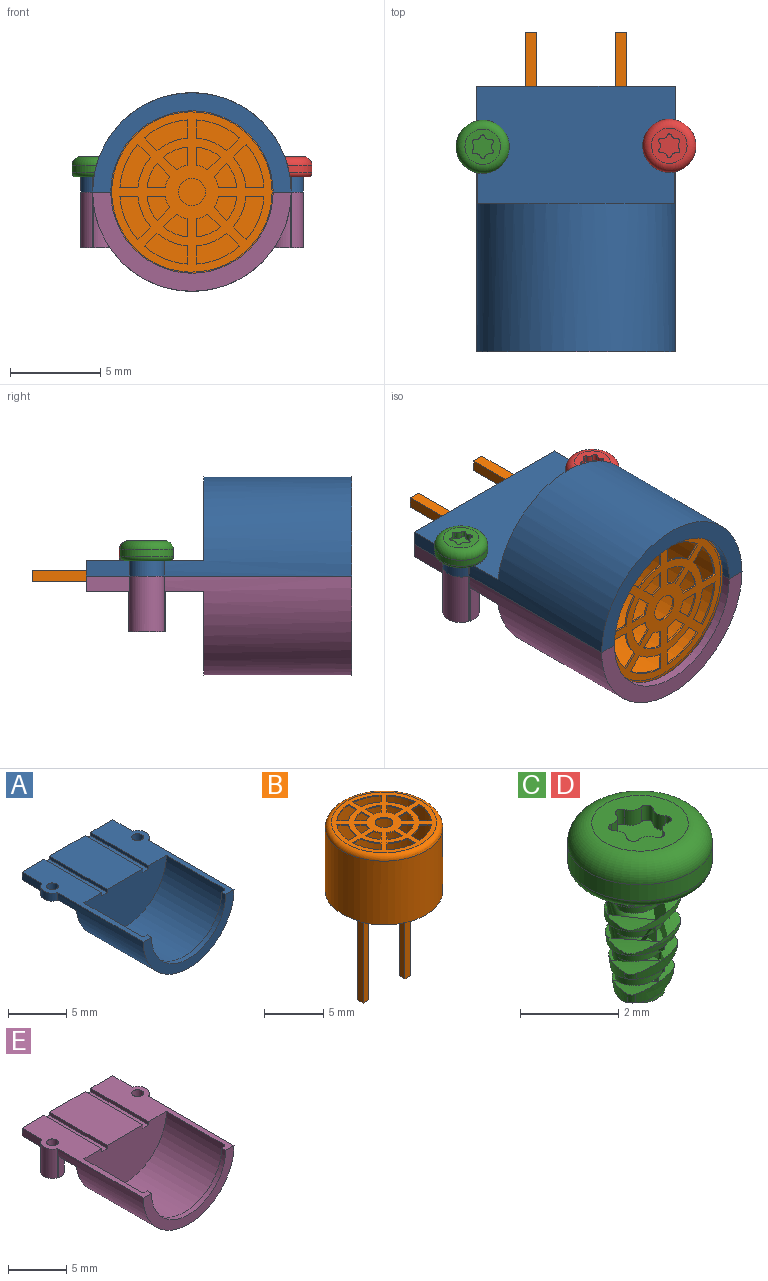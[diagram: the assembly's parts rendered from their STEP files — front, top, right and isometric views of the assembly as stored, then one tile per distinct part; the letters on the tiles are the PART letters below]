
ASSEMBLY  parts=5 mates=4
PART A: 27 faces, bbox 12.4x14.7x5.5 mm
  f0: plane 14.7x3.34mm, normal (0,0,1), area 22.9mm2, adj f4,f5,f6,f7,f8,f9,f13,f16
  f1: plane 7x4.33mm, normal (0,0,1), area 30.3mm2, adj f6,f10,f14,f26
  f2: plane 12.35x6.5mm, normal (0,0,-1), area 71.5mm2, adj f16,f17,f18,f19,f20,f21,f22,f23
  f3: plane 14.7x3.34mm, normal (0,0,1), area 22.9mm2, adj f4,f5,f6,f7,f8,f9,f11,f16
  f4: plane 11x5.5mm, normal (0,-1,0), area 15.7mm2, adj f0,f3,f9,f16
  f5: plane 9.6x4.8mm, normal (0,1,0), area 4.4mm2, adj f0,f3,f8,f9
  f6: plane 10x5mm, normal (0,-1,0), area 38.8mm2, adj f0,f1,f3,f7,f10,f11,f12,f13
  f7: cylinder r=5mm len=10mm, axis (0,1,0), area 110mm2, adj f0,f3,f6,f8
  f8: torus R=4.8mm, axis (0,1,0), area 4.9mm2, adj f0,f3,f5,f7
  f9: cylinder r=4.5mm len=9mm, axis (0,-1,0), area 7.1mm2, adj f0,f3,f4,f5
  f10: plane 7x0.34mm, normal (1,0,0), area 2.3mm2, adj f1,f6,f12,f26
  f11: plane 7x0.34mm, normal (-1,0,0), area 2.3mm2, adj f3,f6,f12,f26
  f12: plane 7x0.67mm, normal (0,0,1), area 4.7mm2, adj f6,f10,f11,f26
  f13: plane 7x0.34mm, normal (1,0,0), area 2.3mm2, adj f0,f6,f15,f26
  f14: plane 7x0.34mm, normal (-1,0,0), area 2.3mm2, adj f1,f6,f15,f26
  f15: plane 7x0.67mm, normal (0,0,1), area 4.7mm2, adj f6,f13,f14,f26
  f16: cylinder r=5.5mm len=11mm, axis (0,-1,0), area 145.4mm2, adj f0,f2,f3,f4,f17,f24,f25
  f17: plane 10.87x4.67mm, normal (0,1,0), area 38.4mm2, adj f2,f16
  f18: plane 2.4x0.84mm, normal (1,0,0), area 2mm2, adj f2,f3,f19,f26
  f19: cylinder r=1.01mm len=1.9mm, axis (0,0,1), area 2.1mm2, adj f2,f3,f18,f25
  f20: plane 2.4x0.84mm, normal (-1,0,0), area 2mm2, adj f0,f2,f21,f26
  f21: cylinder r=1.01mm len=1.9mm, axis (0,0,1), area 2.1mm2, adj f0,f2,f20,f24
  f22: cylinder r=0.51mm len=1.02mm, axis (0,0,1), area 2.7mm2, adj f2,f3
  f23: cylinder r=0.51mm len=1.02mm, axis (0,0,1), area 2.7mm2, adj f0,f2
  f24: plane 0.84x0.06mm, normal (0,-1,0), area 0mm2, adj f2,f16,f21
  f25: plane 0.84x0.06mm, normal (0,-1,0), area 0mm2, adj f2,f16,f19
  f26: plane 11x0.84mm, normal (0,1,0), area 8.7mm2, adj f0,f1,f2,f3,f10,f11,f12,f13
PART B: 99 faces, bbox 10.7x10.7x17.1 mm
  f0: plane 8.88x8.88mm, normal (0,0,1), area 33.7mm2, adj f5,f34,f35,f36,f37,f38,f39,f40
  f1: plane 8.88x8.88mm, normal (0,0,-1), area 33.7mm2, adj f22,f34,f35,f36,f37,f38,f39,f40
  f2: plane 3.5x0.39mm, normal (0,0,-1), area 0.3mm2, adj f3,f6,f20
  f3: cylinder r=4.95mm len=9.9mm, axis (0,0,-1), area 204.3mm2, adj f2,f4,f5,f6,f7,f8
  f4: plane 3.5x0.88mm, normal (0,0,-1), area 2.1mm2, adj f3,f7
  f5: torus R=4.44mm, axis (0,0,1), area 23.9mm2, adj f0,f3
  f6: cylinder r=3mm len=3.5mm, axis (0,0,1), area 0.4mm2, adj f2,f3,f8,f19
  f7: cylinder r=3mm len=3.5mm, axis (0,0,1), area 0.4mm2, adj f3,f4,f8
  f8: plane 9.9x9.26mm, normal (0,0,-1), area 72mm2, adj f3,f6,f7,f10,f11,f12,f13,f15
  f9: plane 0.64x0.64mm, normal (0,0,-1), area 0.4mm2, adj f10,f11,f12,f13
  f10: plane 10x0.64mm, normal (-1,0,0), area 6.4mm2, adj f8,f9,f11,f13
  f11: plane 10x0.64mm, normal (0,-1,0), area 6.4mm2, adj f8,f9,f10,f12
  f12: plane 10x0.64mm, normal (1,0,0), area 6.4mm2, adj f8,f9,f11,f13
  f13: plane 10x0.64mm, normal (0,1,0), area 6.4mm2, adj f8,f9,f10,f12
  f14: plane 0.64x0.64mm, normal (0,0,-1), area 0.4mm2, adj f15,f16,f17,f18
  f15: plane 10x0.64mm, normal (-1,0,0), area 6.4mm2, adj f8,f14,f16,f18
  f16: plane 10x0.64mm, normal (0,-1,0), area 6.4mm2, adj f8,f14,f15,f17
  f17: plane 10x0.64mm, normal (1,0,0), area 6.4mm2, adj f8,f14,f16,f18
  f18: plane 10x0.64mm, normal (0,1,0), area 6.4mm2, adj f8,f14,f15,f17
  f19: plane 9.7x9.08mm, normal (0,0,1), area 69.7mm2, adj f6,f20,f23,f25,f26,f27,f28,f30
  f20: cylinder r=4.85mm len=9.7mm, axis (0,0,-1), area 197.5mm2, adj f2,f19,f21,f22,f23
  f21: plane 3.53x0.88mm, normal (0,0,1), area 2.1mm2, adj f20,f23
  f22: torus R=4.44mm, axis (0,0,1), area 18.9mm2, adj f1,f20
  f23: cylinder r=3.1mm len=3.53mm, axis (0,0,1), area 0.4mm2, adj f19,f20,f21
  f24: plane 0.44x0.44mm, normal (0,0,1), area 0.2mm2, adj f25,f26,f27,f28
  f25: plane 10x0.44mm, normal (1,0,0), area 4.4mm2, adj f19,f24,f26,f28
  f26: plane 10x0.44mm, normal (0,1,0), area 4.4mm2, adj f19,f24,f25,f27
  f27: plane 10x0.44mm, normal (-1,0,0), area 4.4mm2, adj f19,f24,f26,f28
  f28: plane 10x0.44mm, normal (0,-1,0), area 4.4mm2, adj f19,f24,f25,f27
  f29: plane 0.44x0.44mm, normal (0,0,1), area 0.2mm2, adj f30,f31,f32,f33
  f30: plane 10x0.44mm, normal (1,0,0), area 4.4mm2, adj f19,f29,f31,f33
  f31: plane 10x0.44mm, normal (0,1,0), area 4.4mm2, adj f19,f29,f30,f32
  f32: plane 10x0.44mm, normal (-1,0,0), area 4.4mm2, adj f19,f29,f31,f33
  f33: plane 10x0.44mm, normal (0,-1,0), area 4.4mm2, adj f19,f29,f30,f32
  f34: cylinder r=4mm len=2.4mm, axis (0,0,1), area 0.3mm2, adj f0,f1,f35,f37
  f35: plane 1x0.1mm, normal (0,1,0), area 0.1mm2, adj f0,f1,f34,f36
  f36: cylinder r=3mm len=1.69mm, axis (0,0,1), area 0.2mm2, adj f0,f1,f35,f37
  f37: plane 0.71x0.71mm, normal (-0.71,-0.71,0), area 0.1mm2, adj f0,f1,f34,f36
  f38: cylinder r=1.5mm len=0.62mm, axis (0,0,1), area 0.1mm2, adj f0,f1,f39,f41
  f39: plane 1.01x0.1mm, normal (0,1,0), area 0.1mm2, adj f0,f1,f38,f40
  f40: cylinder r=2.5mm len=1.33mm, axis (0,0,1), area 0.1mm2, adj f0,f1,f39,f41
  f41: plane 0.71x0.71mm, normal (0.71,-0.71,0), area 0.1mm2, adj f0,f1,f38,f40
  f42: cylinder r=1.5mm len=0.62mm, axis (0,0,1), area 0.1mm2, adj f0,f1,f43,f45
  f43: plane 0.71x0.71mm, normal (0.71,0.71,0), area 0.1mm2, adj f0,f1,f42,f44
  f44: cylinder r=2.5mm len=1.33mm, axis (0,0,1), area 0.1mm2, adj f0,f1,f43,f45
  f45: plane 1.01x0.1mm, normal (0,-1,0), area 0.1mm2, adj f0,f1,f42,f44
  f46: cylinder r=1.5mm len=0.62mm, axis (0,0,1), area 0.1mm2, adj f0,f1,f47,f49
  f47: plane 1.01x0.1mm, normal (1,0,0), area 0.1mm2, adj f0,f1,f46,f48
  f48: cylinder r=2.5mm len=1.33mm, axis (0,0,1), area 0.1mm2, adj f0,f1,f47,f49
  f49: plane 0.71x0.71mm, normal (-0.71,-0.71,0), area 0.1mm2, adj f0,f1,f46,f48
  f50: plane 1.01x0.1mm, normal (-1,0,0), area 0.1mm2, adj f0,f1,f51,f53
  f51: cylinder r=1.5mm len=0.62mm, axis (0,0,1), area 0.1mm2, adj f0,f1,f50,f52
  f52: plane 0.71x0.71mm, normal (0.71,-0.71,0), area 0.1mm2, adj f0,f1,f51,f53
  f53: cylinder r=2.5mm len=1.33mm, axis (0,0,1), area 0.1mm2, adj f0,f1,f50,f52
  f54: cylinder r=0.75mm len=1.5mm, axis (0,0,1), area 0.5mm2, adj f0,f1
  f55: plane 0.71x0.71mm, normal (-0.71,-0.71,0), area 0.1mm2, adj f0,f1,f56,f58
  f56: cylinder r=2.5mm len=1.33mm, axis (0,0,1), area 0.1mm2, adj f0,f1,f55,f57
  f57: plane 1.01x0.1mm, normal (0,1,0), area 0.1mm2, adj f0,f1,f56,f58
  f58: cylinder r=1.5mm len=0.62mm, axis (0,0,1), area 0.1mm2, adj f0,f1,f55,f57
  f59: cylinder r=2.5mm len=1.33mm, axis (0,0,1), area 0.1mm2, adj f0,f1,f60,f62
  f60: plane 0.71x0.71mm, normal (0.71,0.71,0), area 0.1mm2, adj f0,f1,f59,f61
  f61: cylinder r=1.5mm len=0.62mm, axis (0,0,1), area 0.1mm2, adj f0,f1,f60,f62
  f62: plane 1.01x0.1mm, normal (-1,0,0), area 0.1mm2, adj f0,f1,f59,f61
  f63: cylinder r=1.5mm len=0.62mm, axis (0,0,1), area 0.1mm2, adj f0,f1,f64,f66
  f64: plane 0.71x0.71mm, normal (-0.71,0.71,0), area 0.1mm2, adj f0,f1,f63,f65
  f65: cylinder r=2.5mm len=1.33mm, axis (0,0,1), area 0.1mm2, adj f0,f1,f64,f66
  f66: plane 1.01x0.1mm, normal (1,0,0), area 0.1mm2, adj f0,f1,f63,f65
  f67: plane 1x0.1mm, normal (0,-1,0), area 0.1mm2, adj f0,f1,f68,f70
  f68: cylinder r=3mm len=1.69mm, axis (0,0,1), area 0.2mm2, adj f0,f1,f67,f69
  f69: plane 0.71x0.71mm, normal (0.71,0.71,0), area 0.1mm2, adj f0,f1,f68,f70
  f70: cylinder r=4mm len=2.4mm, axis (0,0,1), area 0.3mm2, adj f0,f1,f67,f69
  f71: cylinder r=3mm len=1.69mm, axis (0,0,1), area 0.2mm2, adj f0,f1,f72,f74
  f72: plane 1x0.1mm, normal (0,1,0), area 0.1mm2, adj f0,f1,f71,f73
  f73: cylinder r=4mm len=2.4mm, axis (0,0,1), area 0.3mm2, adj f0,f1,f72,f74
  f74: plane 0.71x0.71mm, normal (0.71,-0.71,0), area 0.1mm2, adj f0,f1,f71,f73
  f75: cylinder r=4mm len=2.4mm, axis (0,0,1), area 0.3mm2, adj f0,f1,f76,f78
  f76: plane 1x0.1mm, normal (1,0,0), area 0.1mm2, adj f0,f1,f75,f77
  f77: cylinder r=3mm len=1.69mm, axis (0,0,1), area 0.2mm2, adj f0,f1,f76,f78
  f78: plane 0.71x0.71mm, normal (-0.71,0.71,0), area 0.1mm2, adj f0,f1,f75,f77
  f79: plane 1x0.1mm, normal (-1,0,0), area 0.1mm2, adj f0,f1,f80,f82
  f80: cylinder r=4mm len=2.4mm, axis (0,0,1), area 0.3mm2, adj f0,f1,f79,f81
  f81: plane 0.71x0.71mm, normal (0.71,0.71,0), area 0.1mm2, adj f0,f1,f80,f82
  f82: cylinder r=3mm len=1.69mm, axis (0,0,1), area 0.2mm2, adj f0,f1,f79,f81
  f83: plane 1x0.1mm, normal (0,-1,0), area 0.1mm2, adj f0,f1,f84,f86
  f84: cylinder r=4mm len=2.4mm, axis (0,0,1), area 0.3mm2, adj f0,f1,f83,f85
  f85: plane 0.71x0.71mm, normal (-0.71,0.71,0), area 0.1mm2, adj f0,f1,f84,f86
  f86: cylinder r=3mm len=1.69mm, axis (0,0,1), area 0.2mm2, adj f0,f1,f83,f85
  f87: cylinder r=2.5mm len=1.33mm, axis (0,0,1), area 0.1mm2, adj f0,f1,f88,f90
  f88: plane 0.71x0.71mm, normal (-0.71,0.71,0), area 0.1mm2, adj f0,f1,f87,f89
  f89: cylinder r=1.5mm len=0.62mm, axis (0,0,1), area 0.1mm2, adj f0,f1,f88,f90
  f90: plane 1.01x0.1mm, normal (0,-1,0), area 0.1mm2, adj f0,f1,f87,f89
  f91: plane 0.71x0.71mm, normal (0.71,-0.71,0), area 0.1mm2, adj f0,f1,f92,f94
  f92: cylinder r=4mm len=2.4mm, axis (0,0,1), area 0.3mm2, adj f0,f1,f91,f93
  f93: plane 1x0.1mm, normal (-1,0,0), area 0.1mm2, adj f0,f1,f92,f94
  f94: cylinder r=3mm len=1.69mm, axis (0,0,1), area 0.2mm2, adj f0,f1,f91,f93
  f95: plane 0.71x0.71mm, normal (-0.71,-0.71,0), area 0.1mm2, adj f0,f1,f96,f98
  f96: cylinder r=3mm len=1.69mm, axis (0,0,1), area 0.2mm2, adj f0,f1,f95,f97
  f97: plane 1x0.1mm, normal (1,0,0), area 0.1mm2, adj f0,f1,f96,f98
  f98: cylinder r=4mm len=2.4mm, axis (0,0,1), area 0.3mm2, adj f0,f1,f95,f97
PART C: 55 faces, bbox 3.3x3.3x4.4 mm
  f0: cone r=0.34mm half-angle=7deg, axis (0,0,1), area 0mm2, adj f24,f25,f49,f52
  f1: cone r=0.34mm half-angle=7deg, axis (0,0,1), area 0mm2, adj f24,f25,f45,f48
  f2: cylinder r=0.34mm len=0.29mm, axis (0,0,1), area 0mm2, adj f24,f25,f35,f37
  f3: cylinder r=0.34mm len=0.29mm, axis (0,0,1), area 0mm2, adj f24,f25,f31,f38
  f4: cylinder r=0.34mm len=0.29mm, axis (0,0,1), area 0mm2, adj f24,f25,f26,f39
  f5: cylinder r=0.13mm len=0.37mm, axis (0,0,1), area 0.1mm2, adj f13,f17,f20,f21
  f6: cylinder r=0.13mm len=0.37mm, axis (0,0,1), area 0.1mm2, adj f13,f17,f19,f20
  f7: cylinder r=0.13mm len=0.37mm, axis (0,0,1), area 0.1mm2, adj f13,f17,f18,f19
  f8: cylinder r=0.13mm len=0.37mm, axis (0,0,1), area 0.1mm2, adj f13,f16,f17,f18
  f9: torus R=0.98mm, axis (0,0,-1), area 6.3mm2, adj f10,f13
  f10: cylinder r=1.47mm len=2.95mm, axis (0,0,-1), area 3.7mm2, adj f9,f11
  f11: torus R=1.25mm, axis (0,0,-1), area 3.1mm2, adj f10,f12
  f12: plane 2.57x2.57mm, normal (0,0,-1), area 3.6mm2, adj f11,f24,f25,f27,f36,f37
  f13: plane 1.97x1.97mm, normal (0,0,1), area 2mm2, adj f5,f6,f7,f8,f9,f14,f15,f16
  f14: cylinder r=0.26mm len=0.37mm, axis (0,0,1), area 0.1mm2, adj f13,f15,f17,f22
  f15: cylinder r=0.13mm len=0.37mm, axis (0,0,1), area 0.1mm2, adj f13,f14,f16,f17
  f16: cylinder r=0.26mm len=0.37mm, axis (0,0,1), area 0.1mm2, adj f8,f13,f15,f17
  f17: plane 1.31x1.17mm, normal (0,0,1), area 1mm2, adj f5,f6,f7,f8,f14,f15,f16,f18
  f18: cylinder r=0.26mm len=0.37mm, axis (0,0,1), area 0.1mm2, adj f7,f8,f13,f17
  f19: cylinder r=0.26mm len=0.37mm, axis (0,0,1), area 0.1mm2, adj f6,f7,f13,f17
  f20: cylinder r=0.26mm len=0.37mm, axis (0,0,1), area 0.1mm2, adj f5,f6,f13,f17
  f21: cylinder r=0.26mm len=0.37mm, axis (0,0,1), area 0.1mm2, adj f5,f13,f17,f22
  f22: cylinder r=0.13mm len=0.37mm, axis (0,0,1), area 0.1mm2, adj f13,f14,f17,f21
  f23: plane 1.18x1.17mm, normal (0,0,-1), area 0.9mm2, adj f24,f25,f27,f40,f42,f44
  f24: bspline ~3.3x1.63mm, area 4.7mm2, adj f0,f1,f2,f3,f4,f12,f23,f26
  f25: bspline ~3.3x1.96mm, area 4.7mm2, adj f0,f1,f2,f3,f4,f12,f23,f26
  f26: cylinder r=1.22mm len=1.03mm, axis (0,0,1), area 0.1mm2, adj f4,f24,f25,f53
  f27: cylinder r=0.51mm len=3mm, axis (0,0,1), area 2.9mm2, adj f12,f23,f24,f25
  f28: cylinder r=0.34mm len=0.34mm, axis (0,0,1), area 0mm2, adj f24,f25,f29,f39
  f29: cylinder r=1.22mm len=1.05mm, axis (0,0,1), area 0.2mm2, adj f24,f25,f28,f30
  f30: cylinder r=0.34mm len=0.29mm, axis (0,0,1), area 0mm2, adj f24,f25,f29,f31
  f31: cylinder r=1.22mm len=1.22mm, axis (0,0,1), area 0.2mm2, adj f3,f24,f25,f30
  f32: cylinder r=0.34mm len=0.34mm, axis (0,0,1), area 0mm2, adj f24,f25,f33,f38
  f33: cylinder r=1.22mm len=1.05mm, axis (0,0,1), area 0.2mm2, adj f24,f25,f32,f34
  f34: cylinder r=0.34mm len=0.29mm, axis (0,0,1), area 0mm2, adj f24,f25,f33,f35
  f35: cylinder r=1.22mm len=1.22mm, axis (0,0,1), area 0.2mm2, adj f2,f24,f25,f34
  f36: cylinder r=0.34mm len=0.17mm, axis (0,0,1), area 0mm2, adj f12,f25,f37
  f37: cylinder r=1.22mm len=1.05mm, axis (0,0,1), area 0.2mm2, adj f2,f12,f24,f25,f36
  f38: cylinder r=1.22mm len=1.05mm, axis (0,0,1), area 0.2mm2, adj f3,f24,f25,f32
  f39: cylinder r=1.22mm len=1.05mm, axis (0,0,1), area 0.2mm2, adj f4,f24,f25,f28
  f40: cone r=1.22mm half-angle=7deg, axis (0,0,1), area 0.2mm2, adj f23,f24,f25,f42,f46
  f41: cone r=1.22mm half-angle=7deg, axis (0,0,1), area 0.2mm2, adj f24,f25,f43,f47
  f42: cone r=0.34mm half-angle=7deg, axis (0,0,1), area 0mm2, adj f23,f24,f40,f44
  f43: cone r=0.34mm half-angle=7deg, axis (0,0,1), area 0mm2, adj f24,f25,f41,f45
  f44: cone r=1.22mm half-angle=7deg, axis (0,0,1), area 0.1mm2, adj f23,f24,f42
  f45: cone r=1.22mm half-angle=7deg, axis (0,0,1), area 0.2mm2, adj f1,f24,f25,f43
  f46: cone r=0.34mm half-angle=7deg, axis (0,0,1), area 0mm2, adj f24,f25,f40,f48
  f47: cone r=0.34mm half-angle=7deg, axis (0,0,1), area 0mm2, adj f24,f25,f41,f49
  f48: cone r=1.22mm half-angle=7deg, axis (0,0,1), area 0.3mm2, adj f1,f24,f25,f46
  f49: cone r=1.22mm half-angle=7deg, axis (0,0,1), area 0.2mm2, adj f0,f24,f25,f47
  f50: cone r=1.22mm half-angle=7deg, axis (0,0,1), area 0.2mm2, adj f24,f25,f51,f54
  f51: cone r=0.34mm half-angle=7deg, axis (0,0,1), area 0mm2, adj f24,f25,f50,f52
  f52: cone r=1.22mm half-angle=7deg, axis (0,0,1), area 0.2mm2, adj f0,f24,f25,f51
  f53: cone r=1.22mm half-angle=7deg, axis (0,0,1), area 0.1mm2, adj f24,f25,f26,f54
  f54: cone r=0.34mm half-angle=7deg, axis (0,0,1), area 0mm2, adj f24,f25,f50,f53
PART D: same geometry as C
PART E: 33 faces, bbox 12.4x14.7x5.5 mm
  f0: plane 11x6.5mm, normal (0,0,-1), area 66.7mm2, adj f4,f5,f20,f21,f22,f23,f32
  f1: plane 14.7x3.34mm, normal (0,0,1), area 22.9mm2, adj f4,f6,f8,f9,f10,f11,f12,f13
  f2: plane 7x4.33mm, normal (0,0,1), area 30.3mm2, adj f10,f14,f18,f32
  f3: plane 14.7x3.34mm, normal (0,0,1), area 22.9mm2, adj f5,f7,f8,f9,f10,f11,f12,f13
  f4: plane 2.4x0.84mm, normal (1,0,0), area 2mm2, adj f0,f1,f22,f32
  f5: plane 2.4x0.84mm, normal (-1,0,0), area 2mm2, adj f0,f3,f23,f32
  f6: cylinder r=0.51mm len=2.89mm, axis (0,0,1), area 9.2mm2, adj f1,f31
  f7: cylinder r=0.51mm len=2.89mm, axis (0,0,1), area 9.2mm2, adj f3,f30
  f8: plane 11x5.5mm, normal (0,-1,0), area 15.7mm2, adj f1,f3,f13,f20
  f9: plane 9.6x4.8mm, normal (0,1,0), area 4.4mm2, adj f1,f3,f12,f13
  f10: plane 10x5mm, normal (0,-1,0), area 38.8mm2, adj f1,f2,f3,f11,f14,f15,f16,f17
  f11: cylinder r=5mm len=10mm, axis (0,1,0), area 110mm2, adj f1,f3,f10,f12
  f12: torus R=4.8mm, axis (0,1,0), area 4.9mm2, adj f1,f3,f9,f11
  f13: cylinder r=4.5mm len=9mm, axis (0,-1,0), area 7.1mm2, adj f1,f3,f8,f9
  f14: plane 7x0.34mm, normal (1,0,0), area 2.3mm2, adj f2,f10,f16,f32
  f15: plane 7x0.34mm, normal (-1,0,0), area 2.3mm2, adj f1,f10,f16,f32
  f16: plane 7x0.67mm, normal (0,0,1), area 4.7mm2, adj f10,f14,f15,f32
  f17: plane 7x0.34mm, normal (1,0,0), area 2.3mm2, adj f3,f10,f19,f32
  f18: plane 7x0.34mm, normal (-1,0,0), area 2.3mm2, adj f2,f10,f19,f32
  f19: plane 7x0.67mm, normal (0,0,1), area 4.7mm2, adj f10,f17,f18,f32
  f20: cylinder r=5.5mm len=11mm, axis (0,-1,0), area 145.4mm2, adj f0,f1,f3,f8,f21,f24,f25,f26
  f21: plane 10.87x4.67mm, normal (0,1,0), area 38.4mm2, adj f0,f20
  f22: cylinder r=1.01mm len=3.09mm, axis (0,0,1), area 16.2mm2, adj f0,f1,f4,f25,f28,f29
  f23: cylinder r=1.01mm len=3.09mm, axis (0,0,1), area 16.2mm2, adj f0,f3,f5,f24,f26,f27
  f24: plane 3.09x0.06mm, normal (0,-1,0), area 0.2mm2, adj f20,f23,f26,f27
  f25: plane 3.09x0.06mm, normal (0,-1,0), area 0.2mm2, adj f20,f22,f28,f29
  f26: plane 2.25x0.02mm, normal (-1,0,0), area 0mm2, adj f20,f23,f24,f27
  f27: plane 2.02x2.02mm, normal (0,0,-1), area 3.2mm2, adj f23,f24,f26
  f28: plane 2.25x0.02mm, normal (1,0,0), area 0mm2, adj f20,f22,f25,f29
  f29: plane 2.02x2.02mm, normal (0,0,-1), area 3.2mm2, adj f22,f25,f28
  f30: plane 1.02x1.02mm, normal (0,0,1), area 0.8mm2, adj f7
  f31: plane 1.02x1.02mm, normal (0,0,1), area 0.8mm2, adj f6
  f32: plane 11x0.84mm, normal (0,1,0), area 8.7mm2, adj f0,f1,f2,f3,f4,f5,f14,f15
PLACE A rot(axis=(0,1,0),180deg) t=(-10.58,-12.47,25.96)mm
PLACE B rot(axis=(1,0,0),90deg) t=(-18.08,-4.87,10.96)mm
PLACE C t=(-23.25,-1.12,11.8)mm
PLACE D t=(-12.91,-1.06,11.8)mm
PLACE E t=(-25.58,-12.47,-4.04)mm
MATE fastened D.f12 <-> A.f21  axis (0,0,-1) through (-12.92,-1.12,11.8)mm
MATE fastened C.f27 <-> A.f19  axis (0,0,-1) through (-23.25,-1.12,11.8)mm
MATE fastened B.f3 <-> E.f12  axis (0,1,0) through (-18.08,-4.77,10.96)mm
MATE fastened A.f1 <-> E.f2  axis (0,0,-1) through (-18.08,-1.27,10.96)mm
